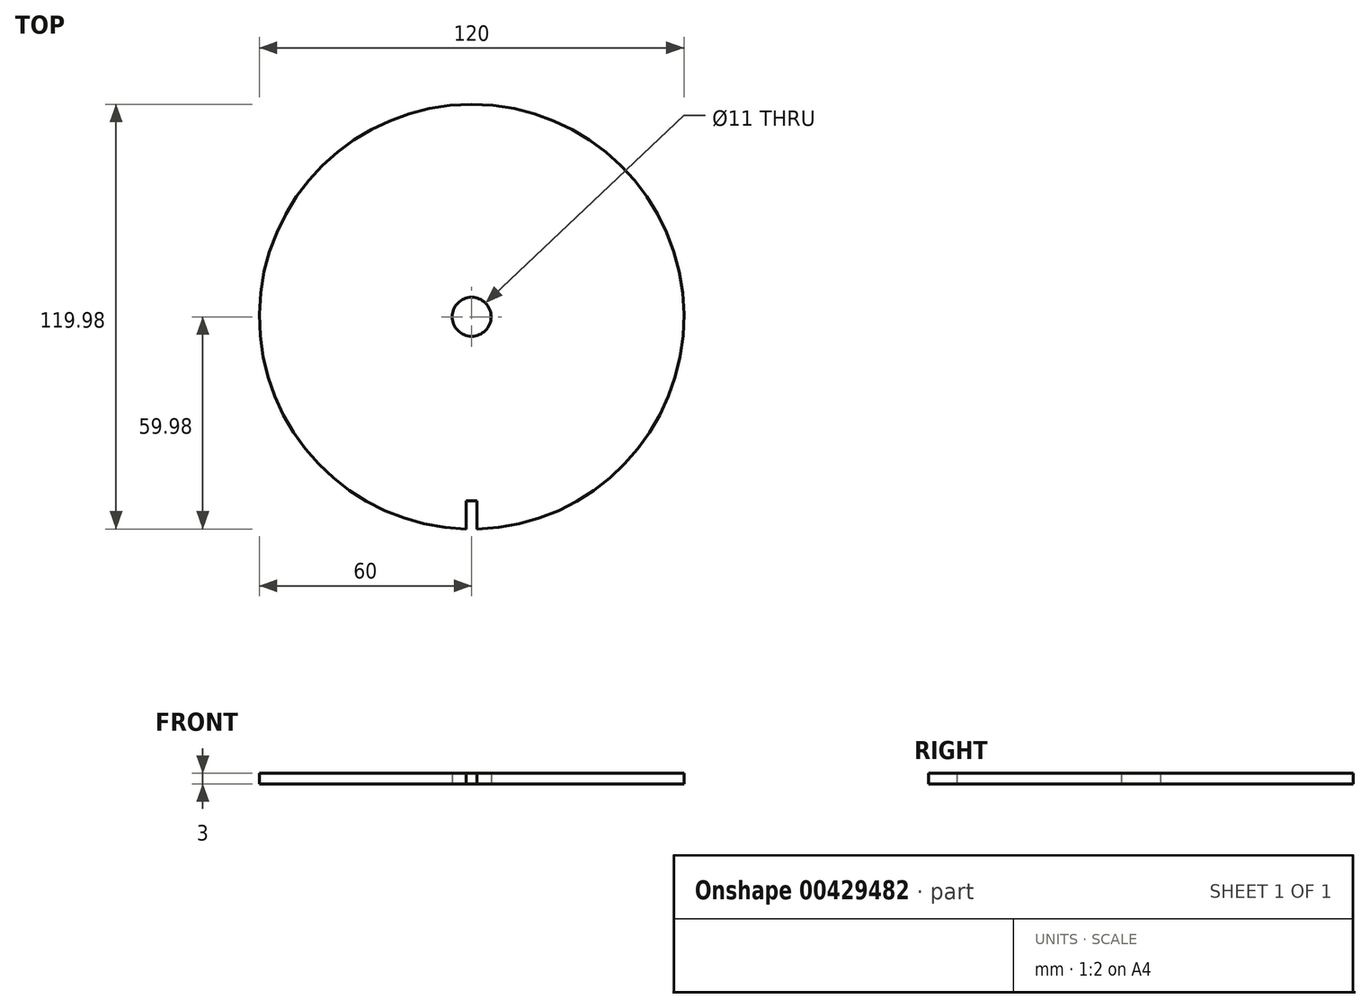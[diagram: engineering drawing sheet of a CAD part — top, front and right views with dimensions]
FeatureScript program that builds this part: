
annotation { "Feature Type Name" : "Feature", "Feature Type Description" : "" }
export const myFeature = defineFeature(function(context is Context, id is Id, definition is map)
    precondition{}
    {
        {
            var Q0;
            Q0=qCreatedBy(makeId("Top.planeOp"),FACE);
            var sketch = newSketch(context, id + "F0", { "sketchPlane" : qUnion([Q0])});
            skCircle(sketch, "E0", {"center": v(0, 0) * mm, "radius": 60 * mm});
            skCircle(sketch, "E1", {"center": v(0, 0) * mm, "radius": 5.5 * mm});
            skSolve(sketch);
        }
        {
            var Q0;
            Q0 = qSketchRegion(id + "F0", true);
            extrude(context, id + "F1", {"entities" : qUnion([Q0]), "depth" : 3 * mm});
        }
        {
            var Q0;
            Q0=qCreatedBy(makeId("Top.planeOp"),FACE);
            var sketch = newSketch(context, id + "F2", { "sketchPlane" : qUnion([Q0])});
            skLineSegment(sketch, "E2", {"start": v(0, 0) * mm, "end": v(0, -60) * mm, "construction": true});
            skLineSegment(sketch, "E3", {"start": v(0, -60) * mm, "end": v(1.5, -60) * mm});
            skLineSegment(sketch, "E4", {"start": v(1.5, -60) * mm, "end": v(1.5, -52) * mm});
            skLineSegment(sketch, "E5", {"start": v(1.5, -52) * mm, "end": v(-1.5, -52) * mm});
            skLineSegment(sketch, "E6", {"start": v(-1.5, -52) * mm, "end": v(-1.5, -60) * mm});
            skLineSegment(sketch, "E7", {"start": v(-1.5, -60) * mm, "end": v(0, -60) * mm});
            skSolve(sketch);
        }
        {
            var Q0;
            Q0 = qSketchRegion(id + "F2", true);
            extrude(context, id + "F3", {"entities" : qUnion([Q0]), "operationType" : NewBodyOperationType.REMOVE, "depth" : 25 * mm});
        }
    });
